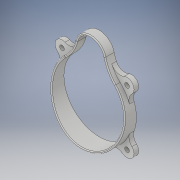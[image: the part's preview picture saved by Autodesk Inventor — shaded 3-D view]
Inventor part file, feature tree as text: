
AUTODESK INVENTOR PART (.ipt)
format: ipt  version: 2018 (Build 220112000, 112)  size: 782,336 bytes
history: native  units: in
note: dims shown in document units (in); Inventor stores cm internally (conversion verified against a paired STEP export)
features: sketch x10, extrude x8, fillet x5, projected_geometry x5, plane x4, loft x2, shell x2, mirror x1, other x1
ambient origin geometry x8: Origin, YZ Plane, XZ Plane, XY Plane, X Axis, Y Axis, Z Axis, Center Point
bodies: Body1 (feature_tree)
feature tree (38):
  sketch  "Sketch2"  dims[d4=4.0in d5=0.825in]
  plane  "Work Plane2"
  loft  "Loft2"
  extrude  "Extrusion1"  Depth=2.0in
  plane  "Work Plane5"
  loft  "Loft6"
  shell  "Shell3"  Thickness=1.125in
  sketch  "Sketch20"  dims[d25=0.25in d26=0.0in d41=0.1in d42=0.75in d55=0.5in]
  extrude  "Extrusion4"  TaperAngle=0.0deg  [1 undecoded]
  extrude  "Extrusion5"  Depth=0.1in
  fillet  "Fillet3"  Radius=0.75in
  fillet  "Fillet4"  Radius=0.5in
  extrude  "Extrusion6"  TaperAngle=0.0deg  [1 undecoded]
  fillet  "Fillet5"  [1 undecoded]
  mirror  "Mirror1"
  fillet  "Fillet6"  Radius=0.1in
  sketch  "Sketch22"  dims[d63=0.125in d64=1.0in d65=0.0in]
  extrude  "Extrusion7"  Depth=1.0in TaperAngle=0.0deg
  extrude  "Extrusion8"  Depth=0.5in
  extrude  "Extrusion9"  Depth=1.75in
  extrude  "Extrusion10"  Depth=1.75in
  fillet  "Fillet7"  Radius=1.5in
  sketch  "Sketch26"  dims[d71=1.5in d72=1.75in d73=1.5in d74=0.25in d75=0.25in d76=0.25in d77=0.0in d78=0.5in d79=0.5in d80=0.0in d81=0.0in d82=0.25in d83=0.0in d84=0.75in d85=0.0in d86=0.5in d87=20.0in d88=0.75in d89=0.0in d90=0.05in]
  shell  "Shell1"  Thickness=0.25in
  plane  "Work Plane3"
  plane  "Work Plane4"
  sketch  "Sketch7"  dims[d6=2.25in d7=2.0in]
  sketch  "Sketch8"  dims[d18=1.0in d19=0.25in d20=1.125in]
  projected_geometry  "Projected Loop1"
  sketch  "Sketch19"  dims[d21=0.0in d22=90.0deg d23=0.0in d24=90.0deg]
  other  "Edges6"
  projected_geometry  "Projected Loop6"
  sketch  "Sketch21"  dims[d56=1.0in d57=0.0in d58=90.0deg d59=0.0in d60=90.0deg d61=0.1in]
  projected_geometry  "Projected Loop7"
  projected_geometry  "Projected Loop8"
  sketch  "Sketch24"  dims[d66=1.0in d67=0.0in d68=0.5in]
  projected_geometry  "Projected Loop9"
  sketch  "Sketch25"  dims[d69=0.5in d70=1.75in]
note: 3 required parameter values undecoded (feature->parameter linkage not recoverable at this tier; creation-order binding heuristic only, values carry confidence <= 0.55)
